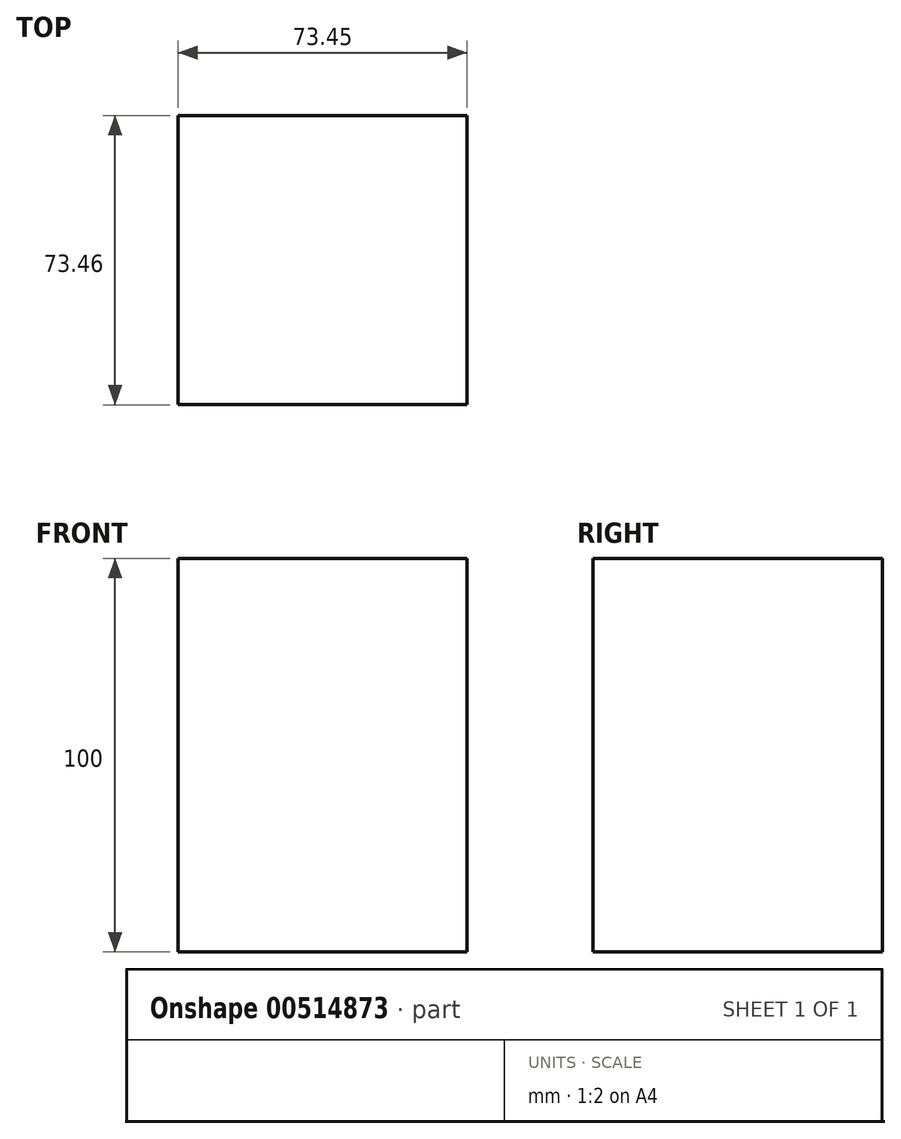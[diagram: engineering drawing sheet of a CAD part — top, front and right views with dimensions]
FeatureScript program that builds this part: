
annotation { "Feature Type Name" : "Feature", "Feature Type Description" : "" }
export const myFeature = defineFeature(function(context is Context, id is Id, definition is map)
    precondition{}
    {
        {
            var Q0;
            Q0=qCreatedBy(makeId("Top.planeOp"),FACE);
            var sketch = newSketch(context, id + "F0", { "sketchPlane" : qUnion([Q0])});
            skLineSegment(sketch, "E0.bottom", {"start": v(0, -2.19) * mm, "end": v(-73.45, -2.19) * mm});
            skLineSegment(sketch, "E0.top", {"start": v(0, 71.27) * mm, "end": v(-73.45, 71.27) * mm});
            skLineSegment(sketch, "E0.left", {"start": v(0, -2.19) * mm, "end": v(0, 71.27) * mm});
            skLineSegment(sketch, "E0.right", {"start": v(-73.45, -2.19) * mm, "end": v(-73.45, 71.27) * mm});
            skSolve(sketch);
        }
        {
            var Q0;
            Q0=makeQuery(id+"F0.imprint","IMPRINT",FACE,{"disambiguationData":[TD([[makeQuery(id+"F0.imprint","IMPRINT",EDGE,{"derivedFrom":sQuery(id+"F0.wireOp",EDGE,"E0.bottom")}),-1.0]])]});
            extrude(context, id + "F1", {"entities" : qUnion([Q0]), "depth" : 100 * mm, "offsetDistance" : 25.4 * mm});
        }
    });
